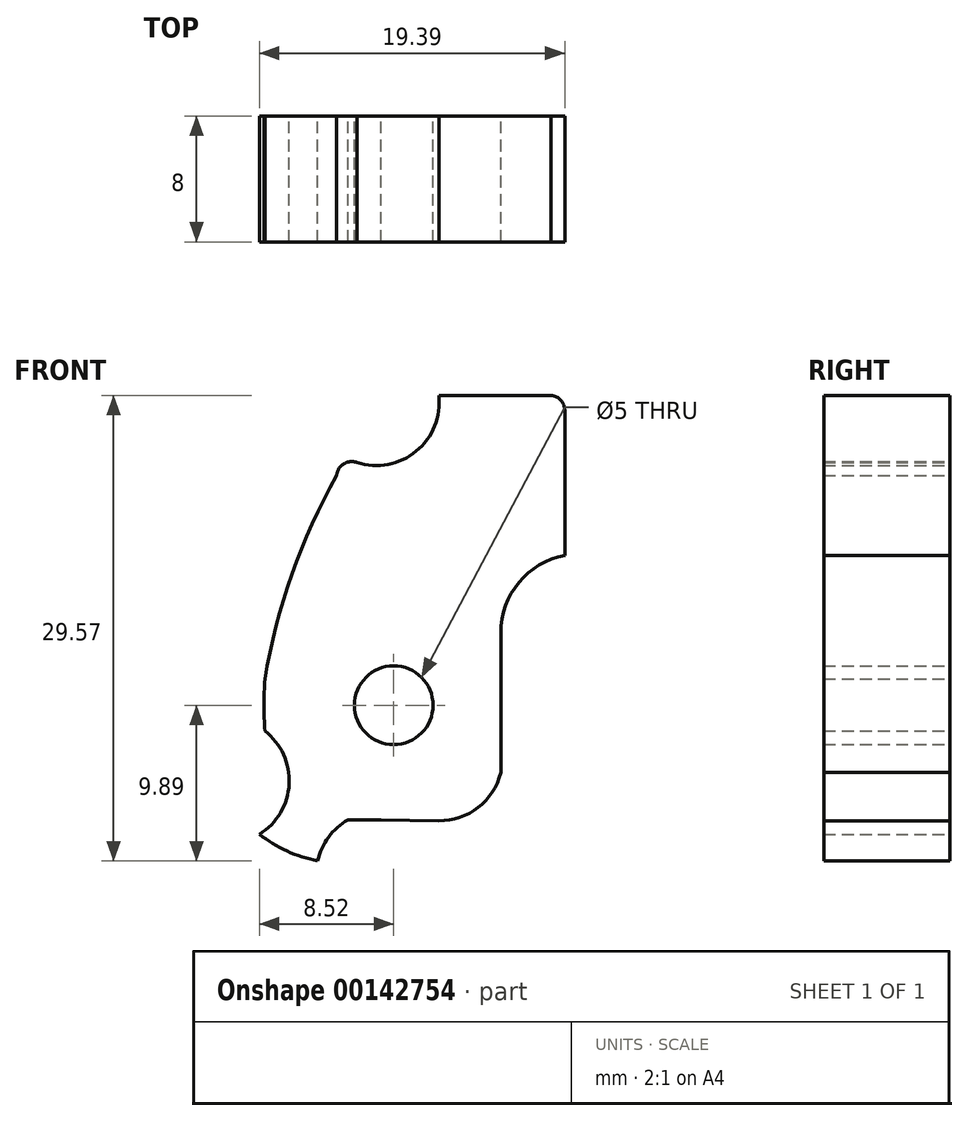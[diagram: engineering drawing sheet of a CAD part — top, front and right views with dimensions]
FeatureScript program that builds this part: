
annotation { "Feature Type Name" : "Feature", "Feature Type Description" : "" }
export const myFeature = defineFeature(function(context is Context, id is Id, definition is map)
    precondition{}
    {
        {
            var Q0;
            Q0=qCreatedBy(makeId("Front.planeOp"),FACE);
            var sketch = newSketch(context, id + "F0", { "sketchPlane" : qUnion([Q0])});
            skCircle(sketch, "E0", {"center": v(0, 0) * mm, "radius": 2.5 * mm});
            skArc(sketch, "E1", {"start": v(2.85, -7.34) * mm, "mid": v(5.36, -6.5) * mm, "end": v(6.8, -4.28) * mm});
            skLineSegment(sketch, "E2", {"start": v(2.85, -7.34) * mm, "end": v(-0.8, -7.28) * mm});
            skLineSegment(sketch, "E3", {"start": v(-0.8, -7.28) * mm, "end": v(-2.9, -7.28) * mm});
            skArc(sketch, "E4", {"start": v(-2.9, -7.28) * mm, "mid": v(-4.14, -8.38) * mm, "end": v(-4.82, -9.89) * mm});
            skArc(sketch, "E5", {"start": v(-8.52, -8.2) * mm, "mid": v(-6.77, -9.26) * mm, "end": v(-4.82, -9.89) * mm});
            skArc(sketch, "E6", {"start": v(-8.52, -8.2) * mm, "mid": v(-6.64, -5) * mm, "end": v(-8.18, -1.63) * mm});
            skArc(sketch, "E7", {"start": v(-8.18, 1.66) * mm, "mid": v(-8.24, 0.01) * mm, "end": v(-8.18, -1.63) * mm});
            skLineSegment(sketch, "E8", {"start": v(10.87, 9.52) * mm, "end": v(10.87, 18.72) * mm});
            skArc(sketch, "E9", {"start": v(10.87, 18.72) * mm, "mid": v(10.62, 19.37) * mm, "end": v(10, 19.68) * mm});
            skArc(sketch, "E10", {"start": v(-3.62, 14.59) * mm, "mid": v(-6.46, 8.32) * mm, "end": v(-8.18, 1.66) * mm});
            skArc(sketch, "E11", {"start": v(-2.33, 15.42) * mm, "mid": v(-3.18, 15.32) * mm, "end": v(-3.62, 14.59) * mm});
            skArc(sketch, "E12", {"start": v(-2.33, 15.42) * mm, "mid": v(1.43, 16.13) * mm, "end": v(2.87, 19.68) * mm});
            skLineSegment(sketch, "E13", {"start": v(10, 19.68) * mm, "end": v(2.87, 19.68) * mm});
            skLineSegment(sketch, "E14", {"start": v(6.8, -4.28) * mm, "end": v(6.8, 4.6) * mm});
            skArc(sketch, "E15", {"start": v(10.87, 9.52) * mm, "mid": v(7.95, 7.8) * mm, "end": v(6.8, 4.6) * mm});
            skSolve(sketch);
        }
        {
            var Q0;
            Q0 = qSketchRegion(id + "F0", true);
            extrude(context, id + "F1", {"entities" : qUnion([Q0]), "endBound" : BoundingType.SYMMETRIC, "depth" : 8 * mm});
        }
    });
